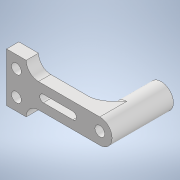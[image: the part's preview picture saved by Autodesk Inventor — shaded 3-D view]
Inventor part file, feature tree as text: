
AUTODESK INVENTOR PART (.ipt)
format: ipt  version: 2020 (Build 240168000, 168)  size: 195,072 bytes
history: native  units: mm
features: extrude x6, sketch x6, projected_geometry x4, other x4, fillet x2, reference x1
ambient origin geometry x8: Origin, YZ Plane, XZ Plane, XY Plane, X Axis, Y Axis, Z Axis, Center Point
bodies: Solid1 (feature_tree)
feature tree (23):
  extrude  "Extrusion1"  Depth=10.0mm TaperAngle=0.0deg
  extrude  "Extrusion2"  Depth=10.0mm
  extrude  "Extrusion3"  Depth=5.0mm TaperAngle=0.0deg
  fillet  "Fillet1"  Radius=6.0mm
  extrude  "Extrusion4"  Depth=8.0mm
  extrude  "Extrusion5"  Depth=5.0mm TaperAngle=0.0deg
  fillet  "Fillet2"  Radius=5.0mm
  extrude  "Extrusion6"  Depth=3.0mm
  sketch  "Sketch1"  dims[d0=10.0mm d1=20.0mm d2=0.0mm]
  reference  "Reference1"
  sketch  "Sketch2"  dims[d3=30.0mm d4=10.0mm]
  projected_geometry  "Projected Loop1"
  sketch  "Sketch3"  dims[d5=5.0mm d6=0.0mm d7=5.0mm d8=0.0mm d9=6.0mm]
  sketch  "Sketch4"  dims[d10=4.0mm d11=8.0mm]
  projected_geometry  "Projected Loop2"
  sketch  "Sketch5"  dims[d12=20.0mm d13=5.0mm d14=0.0mm d15=5.0mm]
  projected_geometry  "Projected Loop3"
  sketch  "Sketch6"  dims[d16=5.0mm d17=4.0mm d18=4.0mm d19=5.0mm d20=0.0mm d21=5.0mm d22=17.0mm d23=6.0mm d24=3.0mm d25=8.0mm d26=0.0mm]
  projected_geometry  "Projected Loop4"
  parser-record x1  (decoder bookkeeping rows leaked as tree rows — omitted from the tree; the rows remain in map.json)
  other  "delta_1.iam"
  other  "arm_shift_1:3"
  other  "motor_holder_1:1"
note: 1 file-system path scrubbed to <path> (originals preserved in map.json)
